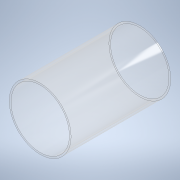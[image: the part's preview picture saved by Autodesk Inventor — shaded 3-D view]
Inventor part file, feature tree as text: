
AUTODESK INVENTOR PART (.ipt)
format: ipt  version: 2022 (Build 260153000, 153)  size: 120,320 bytes
history: native  units: in
note: dims shown in document units (in); Inventor stores cm internally (conversion verified against a paired STEP export)
features: extrude x1, sketch x1, other x1
ambient origin geometry x8: Origin, YZ Plane, XZ Plane, XY Plane, X Axis, Y Axis, Z Axis, Center Point
bodies: Solid1 (feature_tree)
feature tree (3):
  extrude  "Extrusion1"  [1 undecoded]
  sketch  "Sketch1"  dims[d0=8.375in d1=0.0in]
  other  "Boss-Extrude1"
note: 1 required parameter value undecoded (feature->parameter linkage not recoverable at this tier; creation-order binding heuristic only, values carry confidence <= 0.55)
